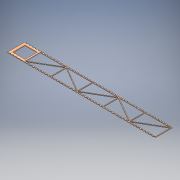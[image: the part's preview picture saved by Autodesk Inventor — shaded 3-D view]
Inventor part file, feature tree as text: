
AUTODESK INVENTOR PART (.ipt)
format: ipt  version: 2018.3 (Build 223284000, 284)  size: 451,072 bytes
history: native  units: mm
features: extrude x4, sketch x4, pattern_linear x2
ambient origin geometry x8: Origin, YZ Plane, XZ Plane, XY Plane, X Axis, Y Axis, Z Axis, Center Point
bodies: Solid1 (feature_tree)
feature tree (10):
  extrude  "Extrusion1"  Depth=40.0mm
  extrude  "Extrusion2"  Depth=1.5875mm TaperAngle=0.0deg
  pattern_linear  "Rectangular Pattern1"  Spacing1=1.5875mm  [1 undecoded]
  extrude  "Extrusion3"  Depth=10.0mm
  pattern_linear  "Rectangular Pattern2"  Spacing1=5.0mm  [1 undecoded]
  extrude  "Extrusion4"  Depth=1.5875mm TaperAngle=0.0deg
  sketch  "Sketch1"  dims[d0=40.0mm d1=40.0mm]
  sketch  "Sketch2"  dims[d7=2.0mm]
  sketch  "Sketch3"  dims[d39=2.0mm d41=2.0mm d48=2.0mm d49=2.0mm d54=2.0mm d55=2.0mm d56=2.0mm d62=1.5875mm d63=0.0mm]
  sketch  "Sketch4"  dims[d64=5.0mm d65=1.5875mm d66=0.0mm d67=480.0mm d69=10.0mm d70=5.0mm d71=1.5875mm d72=0.0mm d73=480.0mm d75=10.0mm d76=1.5875mm d77=0.0mm]
note: 2 required parameter values undecoded (feature->parameter linkage not recoverable at this tier; creation-order binding heuristic only, values carry confidence <= 0.55)
